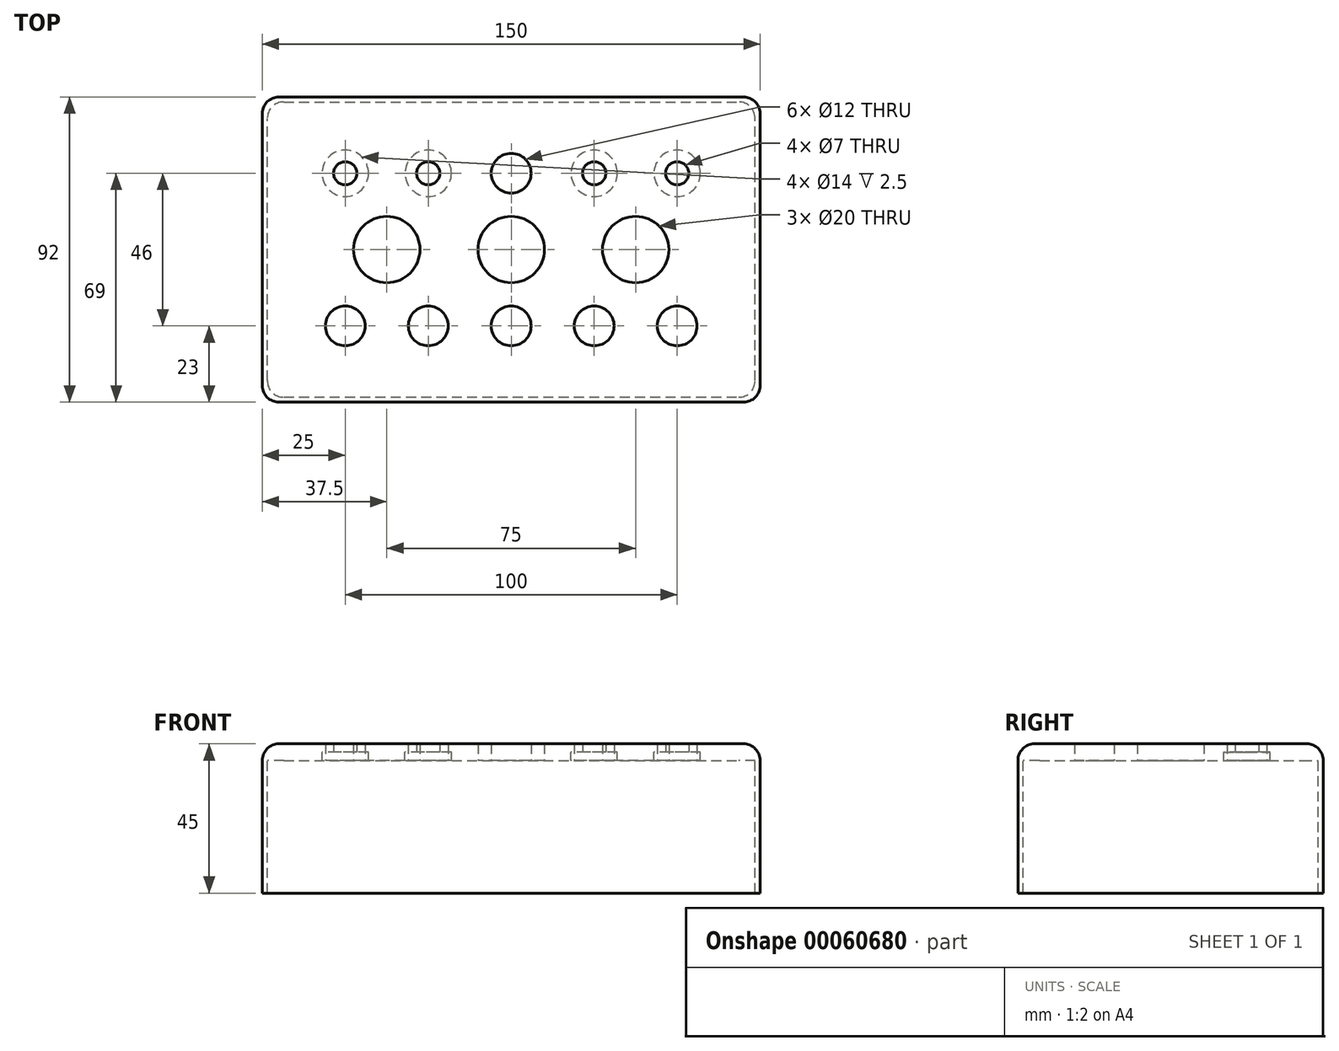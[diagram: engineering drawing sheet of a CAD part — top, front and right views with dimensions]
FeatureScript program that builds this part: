
annotation { "Feature Type Name" : "Feature", "Feature Type Description" : "" }
export const myFeature = defineFeature(function(context is Context, id is Id, definition is map)
    precondition{}
    {
        {
            var Q0;
            Q0=qCreatedBy(makeId("Top.planeOp"),FACE);
            var sketch = newSketch(context, id + "F0", { "sketchPlane" : qUnion([Q0])});
            skLineSegment(sketch, "E0.bottom", {"start": v(-75, 46) * mm, "end": v(75, 46) * mm});
            skLineSegment(sketch, "E0.top", {"start": v(-75, -46) * mm, "end": v(75, -46) * mm});
            skLineSegment(sketch, "E0.left", {"start": v(-75, 46) * mm, "end": v(-75, -46) * mm});
            skLineSegment(sketch, "E0.right", {"start": v(75, 46) * mm, "end": v(75, -46) * mm});
            skCircle(sketch, "E1", {"center": v(-50, 23) * mm, "radius": 3.5 * mm});
            skCircle(sketch, "E2", {"center": v(0, 23) * mm, "radius": 6 * mm});
            skCircle(sketch, "E3", {"center": v(-25, 23) * mm, "radius": 3.5 * mm});
            skCircle(sketch, "E4", {"center": v(25, 23) * mm, "radius": 3.5 * mm});
            skCircle(sketch, "E5", {"center": v(-37.5, 0) * mm, "radius": 10 * mm});
            skCircle(sketch, "E6", {"center": v(0, 0) * mm, "radius": 10 * mm});
            skCircle(sketch, "E7", {"center": v(37.5, 0) * mm, "radius": 10 * mm});
            skCircle(sketch, "E8", {"center": v(-50, -23) * mm, "radius": 6 * mm});
            skCircle(sketch, "E9", {"center": v(-25, -23) * mm, "radius": 6 * mm});
            skCircle(sketch, "E10", {"center": v(0, -23) * mm, "radius": 6 * mm});
            skCircle(sketch, "E11", {"center": v(25, -23) * mm, "radius": 6 * mm});
            skCircle(sketch, "E12", {"center": v(50, -23) * mm, "radius": 6 * mm});
            skCircle(sketch, "E13", {"center": v(50, 23) * mm, "radius": 3.5 * mm});
            skSolve(sketch);
        }
        {
            var Q0;
            Q0=makeQuery(id+"F0.imprint","IMPRINT",FACE,{"disambiguationData":[TD([[makeQuery(id+"F0.imprint","IMPRINT",EDGE,{"derivedFrom":sQuery(id+"F0.wireOp",EDGE,"E0.bottom")}),-1.0]])]});
            extrude(context, id + "F1", {"entities" : qUnion([Q0]), "depth" : 2.5 * mm});
        }
        {
            var Q0;
            Q0=qCreatedBy(makeId("Top.planeOp"),FACE);
            var sketch = newSketch(context, id + "F2", { "sketchPlane" : qUnion([Q0])});
            skLineSegment(sketch, "E14.bottom", {"start": v(-75, 46) * mm, "end": v(75, 46) * mm});
            skLineSegment(sketch, "E14.top", {"start": v(-75, -46) * mm, "end": v(75, -46) * mm});
            skLineSegment(sketch, "E14.left", {"start": v(-75, 46) * mm, "end": v(-75, -46) * mm});
            skLineSegment(sketch, "E14.right", {"start": v(75, 46) * mm, "end": v(75, -46) * mm});
            skCircle(sketch, "E15", {"center": v(-50, 23) * mm, "radius": 7 * mm});
            skCircle(sketch, "E16", {"center": v(0, 23) * mm, "radius": 6 * mm});
            skCircle(sketch, "E17", {"center": v(-25, 23) * mm, "radius": 7 * mm});
            skCircle(sketch, "E18", {"center": v(25, 23) * mm, "radius": 7 * mm});
            skCircle(sketch, "E19", {"center": v(-37.5, 0) * mm, "radius": 10 * mm});
            skCircle(sketch, "E20", {"center": v(0, 0) * mm, "radius": 10 * mm});
            skCircle(sketch, "E21", {"center": v(-50, -23) * mm, "radius": 6 * mm});
            skCircle(sketch, "E22", {"center": v(-25, -23) * mm, "radius": 6 * mm});
            skCircle(sketch, "E23", {"center": v(0, -23) * mm, "radius": 6 * mm});
            skCircle(sketch, "E24", {"center": v(25, -23) * mm, "radius": 6 * mm});
            skCircle(sketch, "E25", {"center": v(50, -23) * mm, "radius": 6 * mm});
            skCircle(sketch, "E26", {"center": v(50, 23) * mm, "radius": 7 * mm});
            skCircle(sketch, "E27", {"center": v(37.5, 0) * mm, "radius": 10 * mm});
            skSolve(sketch);
        }
        {
            var Q0;
            Q0 = qSketchRegion(id + "F2", true);
            extrude(context, id + "F3", {"entities" : qUnion([Q0]), "operationType" : NewBodyOperationType.ADD, "oppositeDirection" : true, "depth" : 2.5 * mm});
        }
        {
            var Q0;
            Q0=makeQuery(id+"F1.opExtrude","CAP_EDGE",EDGE,{"disambiguationData":[OSD([sQuery(id+"F0.wireOp",EDGE,"E0.bottom")])],"isStart":false});
            var Q1;
            Q1=makeQuery(id+"F1.opExtrude","CAP_EDGE",EDGE,{"disambiguationData":[OSD([sQuery(id+"F0.wireOp",EDGE,"E0.left")])],"isStart":false});
            var Q2;
            Q2=makeQuery(id+"F1.opExtrude","CAP_EDGE",EDGE,{"disambiguationData":[OSD([sQuery(id+"F0.wireOp",EDGE,"E0.top")])],"isStart":false});
            var Q3;
            Q3=makeQuery(id+"F1.opExtrude","CAP_EDGE",EDGE,{"disambiguationData":[OSD([sQuery(id+"F0.wireOp",EDGE,"E0.right")])],"isStart":false});
            fillet(context, id + "F4", {"entities" : qUnion([Q0, Q1, Q2, Q3]), "radius" : 5 * mm, "tangentPropagation" : true, "allowEdgeOverflow" : false});
        }
        {
            var Q0;
            Q0=makeQuery(id+"F3.opExtrude","CAP_FACE",FACE,{"disambiguationData":[OSD([sQuery(id+"F2.wireOp",EDGE,"E14.bottom"),sQuery(id+"F2.wireOp",EDGE,"E14.top"),sQuery(id+"F2.wireOp",EDGE,"E14.left"),sQuery(id+"F2.wireOp",EDGE,"E14.right"),sQuery(id+"F2.wireOp",EDGE,"E15"),sQuery(id+"F2.wireOp",EDGE,"E16"),sQuery(id+"F2.wireOp",EDGE,"E17"),sQuery(id+"F2.wireOp",EDGE,"E18"),sQuery(id+"F2.wireOp",EDGE,"E19"),sQuery(id+"F2.wireOp",EDGE,"E20"),sQuery(id+"F2.wireOp",EDGE,"E21"),sQuery(id+"F2.wireOp",EDGE,"E22"),sQuery(id+"F2.wireOp",EDGE,"E23"),sQuery(id+"F2.wireOp",EDGE,"E24"),sQuery(id+"F2.wireOp",EDGE,"E25"),sQuery(id+"F2.wireOp",EDGE,"E26"),sQuery(id+"F2.wireOp",EDGE,"E27")])],"isStart":false});
            var sketch = newSketch(context, id + "F5", { "sketchPlane" : qUnion([Q0])});
            skLineSegment(sketch, "E28.bottom", {"start": v(-75, 46) * mm, "end": v(75, 46) * mm});
            skLineSegment(sketch, "E28.top", {"start": v(-75, -46) * mm, "end": v(75, -46) * mm});
            skLineSegment(sketch, "E28.left", {"start": v(-75, 46) * mm, "end": v(-75, -46) * mm});
            skLineSegment(sketch, "E28.right", {"start": v(75, 46) * mm, "end": v(75, -46) * mm});
            skLineSegment(sketch, "E29.bottom", {"start": v(-68.5, 44.5) * mm, "end": v(68.5, 44.5) * mm});
            skLineSegment(sketch, "E29.top", {"start": v(-68.5, -44.5) * mm, "end": v(68.5, -44.5) * mm});
            skLineSegment(sketch, "E29.left", {"start": v(-73.5, 39.5) * mm, "end": v(-73.5, -39.5) * mm});
            skLineSegment(sketch, "E29.right", {"start": v(73.5, 39.5) * mm, "end": v(73.5, -39.5) * mm});
            skPoint(sketch, "E30.visualSharp", {"position": v(-73.5, 44.5) * mm});
            skArc(sketch, "E30.filletArc", {"start": v(-68.5, 44.5) * mm, "mid": v(-72.04, 43.04) * mm, "end": v(-73.5, 39.5) * mm});
            skPoint(sketch, "E31.visualSharp", {"position": v(73.5, 44.5) * mm});
            skArc(sketch, "E31.filletArc", {"start": v(73.5, 39.5) * mm, "mid": v(72.04, 43.04) * mm, "end": v(68.5, 44.5) * mm});
            skPoint(sketch, "E32.visualSharp", {"position": v(73.5, -44.5) * mm});
            skArc(sketch, "E32.filletArc", {"start": v(68.5, -44.5) * mm, "mid": v(72.04, -43.04) * mm, "end": v(73.5, -39.5) * mm});
            skPoint(sketch, "E33.visualSharp", {"position": v(-73.5, -44.5) * mm});
            skArc(sketch, "E33.filletArc", {"start": v(-73.5, -39.5) * mm, "mid": v(-72.04, -43.04) * mm, "end": v(-68.5, -44.5) * mm});
            skSolve(sketch);
        }
        {
            var Q0;
            Q0=makeQuery(id+"F5.imprint","IMPRINT",FACE,{"disambiguationData":[TD([[makeQuery(id+"F5.imprint","IMPRINT",EDGE,{"derivedFrom":sQuery(id+"F5.wireOp",EDGE,"E28.bottom")}),-1.0]])]});
            extrude(context, id + "F6", {"entities" : qUnion([Q0]), "operationType" : NewBodyOperationType.ADD, "depth" : 40 * mm});
        }
        {
            var Q0;
            Q0=makeQuery(id+"F6.opExtrude","SWEPT_EDGE",EDGE,{"disambiguationData":[OSD([sQuery(id+"F5.wireOp",EDGE,"E28.bottom"),sQuery(id+"F5.wireOp",EDGE,"E28.right")])]});
            var Q1;
            Q1=makeQuery(id+"F6.opExtrude","SWEPT_EDGE",EDGE,{"disambiguationData":[OSD([sQuery(id+"F5.wireOp",EDGE,"E28.top"),sQuery(id+"F5.wireOp",EDGE,"E28.right")])]});
            var Q2;
            Q2=makeQuery(id+"F6.opExtrude","SWEPT_EDGE",EDGE,{"disambiguationData":[OSD([sQuery(id+"F5.wireOp",EDGE,"E28.top"),sQuery(id+"F5.wireOp",EDGE,"E28.left")])]});
            var Q3;
            Q3=makeQuery(id+"F6.opExtrude","SWEPT_EDGE",EDGE,{"disambiguationData":[OSD([sQuery(id+"F5.wireOp",EDGE,"E28.bottom"),sQuery(id+"F5.wireOp",EDGE,"E28.left")])]});
            fillet(context, id + "F7", {"entities" : qUnion([Q0, Q1, Q2, Q3]), "radius" : 5 * mm, "tangentPropagation" : true, "allowEdgeOverflow" : false});
        }
    });
